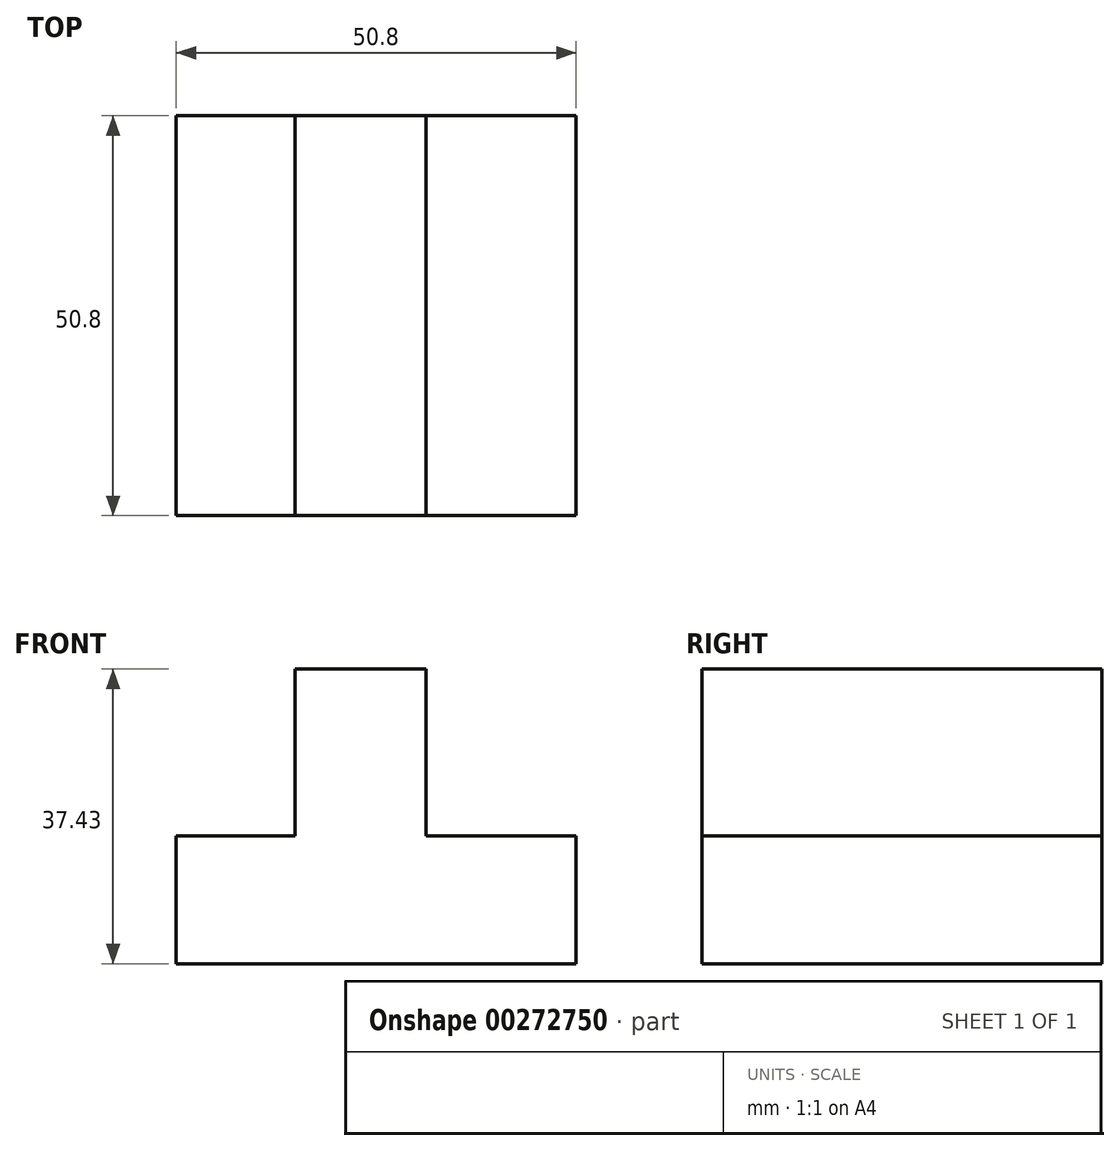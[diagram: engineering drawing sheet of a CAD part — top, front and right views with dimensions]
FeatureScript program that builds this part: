
annotation { "Feature Type Name" : "Feature", "Feature Type Description" : "" }
export const myFeature = defineFeature(function(context is Context, id is Id, definition is map)
    precondition{}
    {
        {
            var Q0;
            Q0=qCreatedBy(makeId("Front.planeOp"),FACE);
            var sketch = newSketch(context, id + "F0", { "sketchPlane" : qUnion([Q0])});
            skLineSegment(sketch, "E0", {"start": v(0, 0) * mm, "end": v(-50.8, 0) * mm});
            skLineSegment(sketch, "E1", {"start": v(-50.8, 0) * mm, "end": v(-50.8, 16.23) * mm});
            skLineSegment(sketch, "E2", {"start": v(-50.8, 16.23) * mm, "end": v(-35.7, 16.23) * mm});
            skLineSegment(sketch, "E3", {"start": v(-35.7, 16.23) * mm, "end": v(-35.7, 37.43) * mm});
            skLineSegment(sketch, "E4", {"start": v(-35.7, 37.43) * mm, "end": v(-19.1, 37.43) * mm});
            skLineSegment(sketch, "E5", {"start": v(-19.1, 37.43) * mm, "end": v(-19.1, 16.23) * mm});
            skLineSegment(sketch, "E6", {"start": v(-19.1, 16.23) * mm, "end": v(0, 16.23) * mm});
            skLineSegment(sketch, "E7", {"start": v(0, 16.23) * mm, "end": v(0, 0) * mm});
            skSolve(sketch);
        }
        {
            var Q0;
            Q0=makeQuery(id+"F0.imprint","IMPRINT",FACE,{"disambiguationData":[TD([[makeQuery(id+"F0.imprint","IMPRINT",EDGE,{"derivedFrom":sQuery(id+"F0.wireOp",EDGE,"E0")}),-1.0]])]});
            extrude(context, id + "F1", {"entities" : qUnion([Q0]), "depth" : 50.8 * mm});
        }
    });
